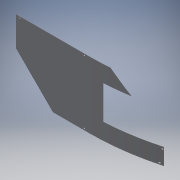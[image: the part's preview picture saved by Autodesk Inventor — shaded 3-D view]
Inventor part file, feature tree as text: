
AUTODESK INVENTOR PART (.ipt)
format: ipt  version: 2016 (Build 200138000, 138)  size: 345,600 bytes
history: native  units: mm
features: reference x15, other x7, sketch x5, sheet_metal_op x3, hole x1
ambient origin geometry x8: Origin, YZ Plane, XZ Plane, XY Plane, X Axis, Y Axis, Z Axis, Center Point
bodies: Solid1 (feature_tree)
feature tree (31):
  sheet_metal_op  "Contour Flange1"
  sketch  "Sketch1"  dims[d0=1.0mm d1=0.5mm]
  reference  "Reference1"
  reference  "Reference2"
  reference  "Reference3"
  other  "Plate1"
  sheet_metal_op  "Bend1"
  sheet_metal_op  "Corner1"
  sketch  "Sketch11"  dims[d2=2.0mm]
  reference  "Reference19"
  sketch  "Sketch12"  dims[d3=1.0mm]
  reference  "Reference24"
  reference  "Reference26"
  sketch  "Sketch13"  dims[d4=309.0mm]
  reference  "Reference27"
  reference  "Reference28"
  reference  "Reference29"
  reference  "Reference30"
  sketch  "Sketch14"  dims[d5=1.0mm d6=0.5mm d7=4.0mm d8=1.0mm d9=1.0mm d13=1.0mm d14=0.0mm d77=1.0mm d78=0.0mm d83=1.0mm d84=0.0mm d85=1.0mm d86=4.0mm d87=2.2mm d88=4.0mm d89=2.2mm d90=4.0mm d91=2.2mm d92=4.0mm d93=2.2mm d94=1.0mm d95=0.0mm d96=4.0mm d97=2.2mm d98=2.0mm d99=2.2mm d100=1.0mm d101=0.0mm d102=156.0mm d103=247.0mm d104=2.2mm d105=2.2mm d106=3.0mm d107=3.0mm d108=3.5mm d10=10.0mm d11=4.0mm d12=6.0mm d15=90.0deg d16=8.0mm d17=20.594885mm]
  reference  "Reference31"
  reference  "Reference32"
  reference  "Reference33"
  reference  "Reference34"
  reference  "Reference35"
  other  "Cut1"
  other  "Cut7"
  other  "Cut8"
  other  "Cut9"
  other  "Cut10"
  other  "Definition1"
  hole  "Hole1"  [1 undecoded]
note: 1 required parameter value undecoded (feature->parameter linkage not recoverable at this tier; creation-order binding heuristic only, values carry confidence <= 0.55)
